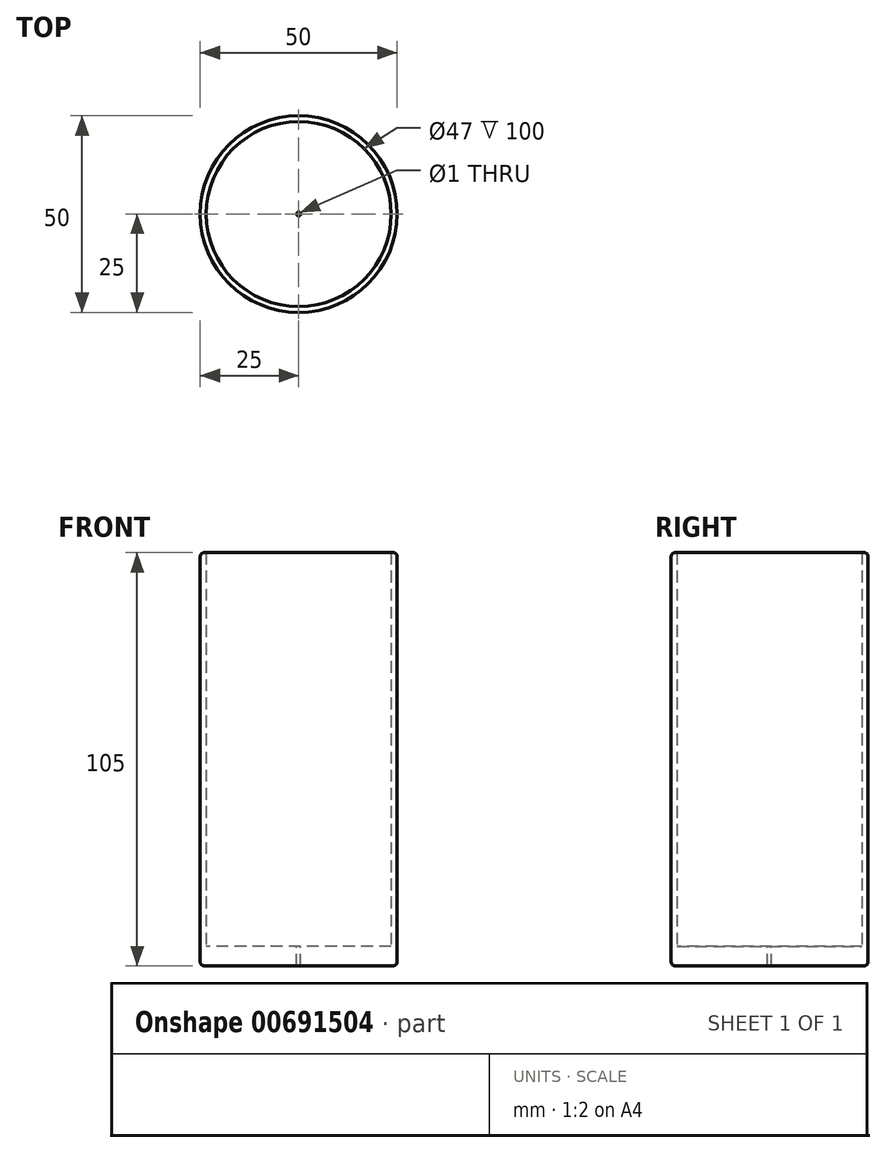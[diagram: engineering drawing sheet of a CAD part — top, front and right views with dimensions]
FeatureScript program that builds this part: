
annotation { "Feature Type Name" : "Feature", "Feature Type Description" : "" }
export const myFeature = defineFeature(function(context is Context, id is Id, definition is map)
    precondition{}
    {
        {
            var Q0;
            Q0=qCreatedBy(makeId("Top.planeOp"),FACE);
            var sketch = newSketch(context, id + "F0", { "sketchPlane" : qUnion([Q0])});
            skCircle(sketch, "E0", {"center": v(0, 0) * mm, "radius": 25 * mm});
            skCircle(sketch, "E1", {"center": v(0, 0) * mm, "radius": 23.5 * mm});
            skSolve(sketch);
        }
        {
            var Q0;
            Q0=makeQuery(id+"F0.imprint","IMPRINT",FACE,{"disambiguationData":[TD([[makeQuery(id+"F0.imprint","IMPRINT",EDGE,{"derivedFrom":sQuery(id+"F0.wireOp",EDGE,"E0")}),1.0]])]});
            extrude(context, id + "F1", {"entities" : qUnion([Q0]), "depth" : 100 * mm, "offsetDistance" : 25 * mm});
        }
        {
            var Q0;
            Q0=qCreatedBy(makeId("Top.planeOp"),FACE);
            var sketch = newSketch(context, id + "F2", { "sketchPlane" : qUnion([Q0])});
            skCircle(sketch, "E2", {"center": v(0, 0) * mm, "radius": 25 * mm});
            skSolve(sketch);
        }
        {
            var Q0;
            Q0=makeQuery(id+"F2.imprint","IMPRINT",FACE,{"disambiguationData":[TD([[makeQuery(id+"F2.imprint","IMPRINT",EDGE,{"derivedFrom":sQuery(id+"F2.wireOp",EDGE,"E2")}),1.0]])]});
            extrude(context, id + "F3", {"entities" : qUnion([Q0]), "operationType" : NewBodyOperationType.ADD, "oppositeDirection" : true, "depth" : 5 * mm, "offsetDistance" : 25 * mm});
        }
        {
            var Q0;
            Q0=makeQuery(id+"F3.opExtrude","CAP_EDGE",EDGE,{"disambiguationData":[OSD([sQuery(id+"F2.wireOp",EDGE,"E2")])],"isStart":false});
            var Q1;
            Q1=makeQuery(id+"F1.opExtrude","CAP_EDGE",EDGE,{"disambiguationData":[OSD([sQuery(id+"F0.wireOp",EDGE,"E0")])],"isStart":false});
            fillet(context, id + "F4", {"entities" : qUnion([Q0, Q1]), "radius" : 1 * mm, "tangentPropagation" : true, "allowEdgeOverflow" : false});
        }
        {
            var Q0;
            Q0=qCreatedBy(makeId("Top.planeOp"),FACE);
            var sketch = newSketch(context, id + "F5", { "sketchPlane" : qUnion([Q0])});
            skCircle(sketch, "E3", {"center": v(0, 0) * mm, "radius": 0.5 * mm});
            skSolve(sketch);
        }
        {
            var Q0;
            Q0=makeQuery(id+"F5.imprint","IMPRINT",FACE,{"disambiguationData":[TD([[makeQuery(id+"F5.imprint","IMPRINT",EDGE,{"derivedFrom":sQuery(id+"F5.wireOp",EDGE,"E3")}),1.0]])]});
            extrude(context, id + "F6", {"entities" : qUnion([Q0]), "operationType" : NewBodyOperationType.REMOVE, "oppositeDirection" : true, "depth" : 25 * mm, "offsetDistance" : 25 * mm});
        }
    });
